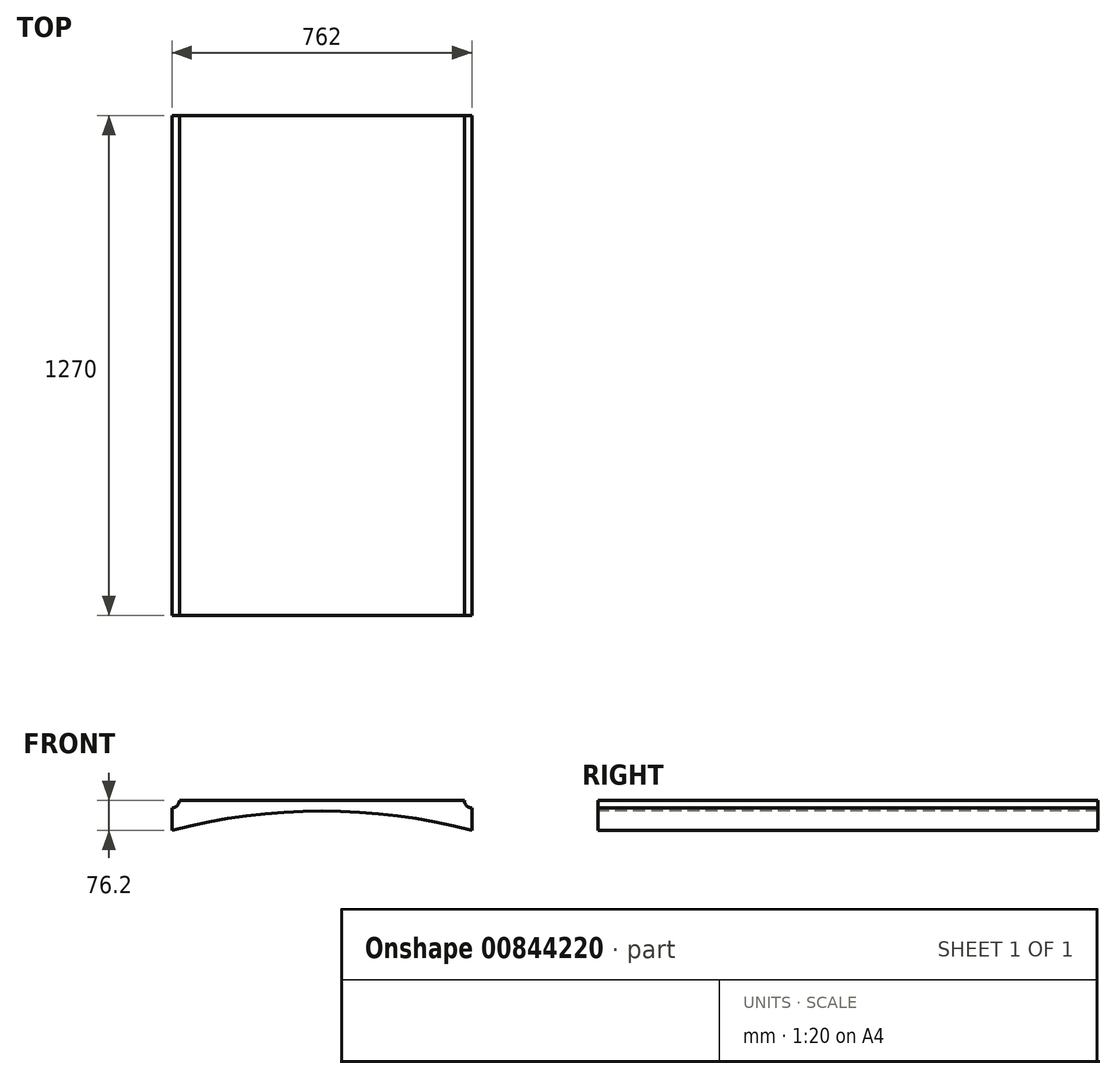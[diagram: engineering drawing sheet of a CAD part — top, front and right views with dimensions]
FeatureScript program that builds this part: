
annotation { "Feature Type Name" : "Feature", "Feature Type Description" : "" }
export const myFeature = defineFeature(function(context is Context, id is Id, definition is map)
    precondition{}
    {
        {
            var Q0;
            Q0=qCreatedBy(makeId("Front.planeOp"),FACE);
            var sketch = newSketch(context, id + "F0", { "sketchPlane" : qUnion([Q0])});
            skLineSegment(sketch, "E0.bottom", {"start": v(381, 38.1) * mm, "end": v(-381, 38.1) * mm});
            skLineSegment(sketch, "E0.top", {"start": v(381, -38.1) * mm, "end": v(-381, -38.1) * mm});
            skLineSegment(sketch, "E0.left", {"start": v(381, 38.1) * mm, "end": v(381, -38.1) * mm});
            skLineSegment(sketch, "E0.right", {"start": v(-381, 38.1) * mm, "end": v(-381, -38.1) * mm});
            skPoint(sketch, "E0.middle", {"position": v(0, 0) * mm});
            skSolve(sketch);
        }
        {
            var Q0;
            Q0 = qSketchRegion(id + "F0", true);
            extrude(context, id + "F1", {"entities" : qUnion([Q0]), "depth" : 1270 * mm, "offsetDistance" : 25.4 * mm});
        }
        {
            var Q0;
            Q0=makeQuery(id+"F1.opExtrude","SWEPT_FACE",FACE,{"disambiguationData":[OSD([sQuery(id+"F0.wireOp",EDGE,"E0.top")])]});
            var sketch = newSketch(context, id + "F2", { "sketchPlane" : qUnion([Q0])});
            skLineSegment(sketch, "E1", {"start": v(0, -522.85) * mm, "end": v(0, 1635.92) * mm, "construction": true});
            skCircle(sketch, "E2", {"center": v(0, 1231.9) * mm, "radius": 12.7 * mm});
            skCircle(sketch, "E3", {"center": v(0, 38.1) * mm, "radius": 12.7 * mm});
            skCircle(sketch, "E4", {"center": v(0, 876.3) * mm, "radius": 38.1 * mm});
            skCircle(sketch, "E5", {"center": v(0, 393.7) * mm, "radius": 38.1 * mm});
            skSolve(sketch);
        }
        {
            var Q0;
            Q0 = qSketchRegion(id + "F2", true);
            extrude(context, id + "F3", {"entities" : qUnion([Q0]), "operationType" : NewBodyOperationType.REMOVE, "oppositeDirection" : true, "depth" : 25.4 * mm, "offsetDistance" : 25.4 * mm});
        }
        {
            var Q0;
            Q0=makeQuery(id+"F1.opExtrude","CAP_FACE",FACE,{"disambiguationData":[OSD([sQuery(id+"F0.wireOp",EDGE,"E0.bottom"),sQuery(id+"F0.wireOp",EDGE,"E0.top"),sQuery(id+"F0.wireOp",EDGE,"E0.left"),sQuery(id+"F0.wireOp",EDGE,"E0.right")])],"isStart":false});
            var sketch = newSketch(context, id + "F4", { "sketchPlane" : qUnion([Q0])});
            skArc(sketch, "E6", {"start": v(381, -38.1) * mm, "mid": v(0, 11) * mm, "end": v(-381, -38.1) * mm});
            skLineSegment(sketch, "E7", {"start": v(-381, -38.1) * mm, "end": v(381, -38.1) * mm});
            skSolve(sketch);
        }
        {
            var Q0;
            Q0 = qSketchRegion(id + "F4", true);
            extrude(context, id + "F5", {"entities" : qUnion([Q0]), "operationType" : NewBodyOperationType.REMOVE, "endBound" : BoundingType.THROUGH_ALL, "oppositeDirection" : true, "depth" : 25.4 * mm, "offsetDistance" : 25.4 * mm});
        }
        {
            var Q0;
            Q0=makeQuery(id+"F1.opExtrude","CAP_FACE",FACE,{"disambiguationData":[OSD([sQuery(id+"F0.wireOp",EDGE,"E0.bottom"),sQuery(id+"F0.wireOp",EDGE,"E0.top"),sQuery(id+"F0.wireOp",EDGE,"E0.left"),sQuery(id+"F0.wireOp",EDGE,"E0.right")])],"isStart":true});
            var sketch = newSketch(context, id + "F6", { "sketchPlane" : qUnion([Q0])});
            skCircle(sketch, "E8", {"center": v(-381, 38.1) * mm, "radius": 19.05 * mm});
            skCircle(sketch, "E9", {"center": v(381, 38.1) * mm, "radius": 19.05 * mm});
            skSolve(sketch);
        }
        {
            var Q0;
            Q0 = qSketchRegion(id + "F6", true);
            extrude(context, id + "F7", {"entities" : qUnion([Q0]), "operationType" : NewBodyOperationType.REMOVE, "endBound" : BoundingType.THROUGH_ALL, "oppositeDirection" : true, "depth" : 25.4 * mm, "offsetDistance" : 25.4 * mm});
        }
    });
